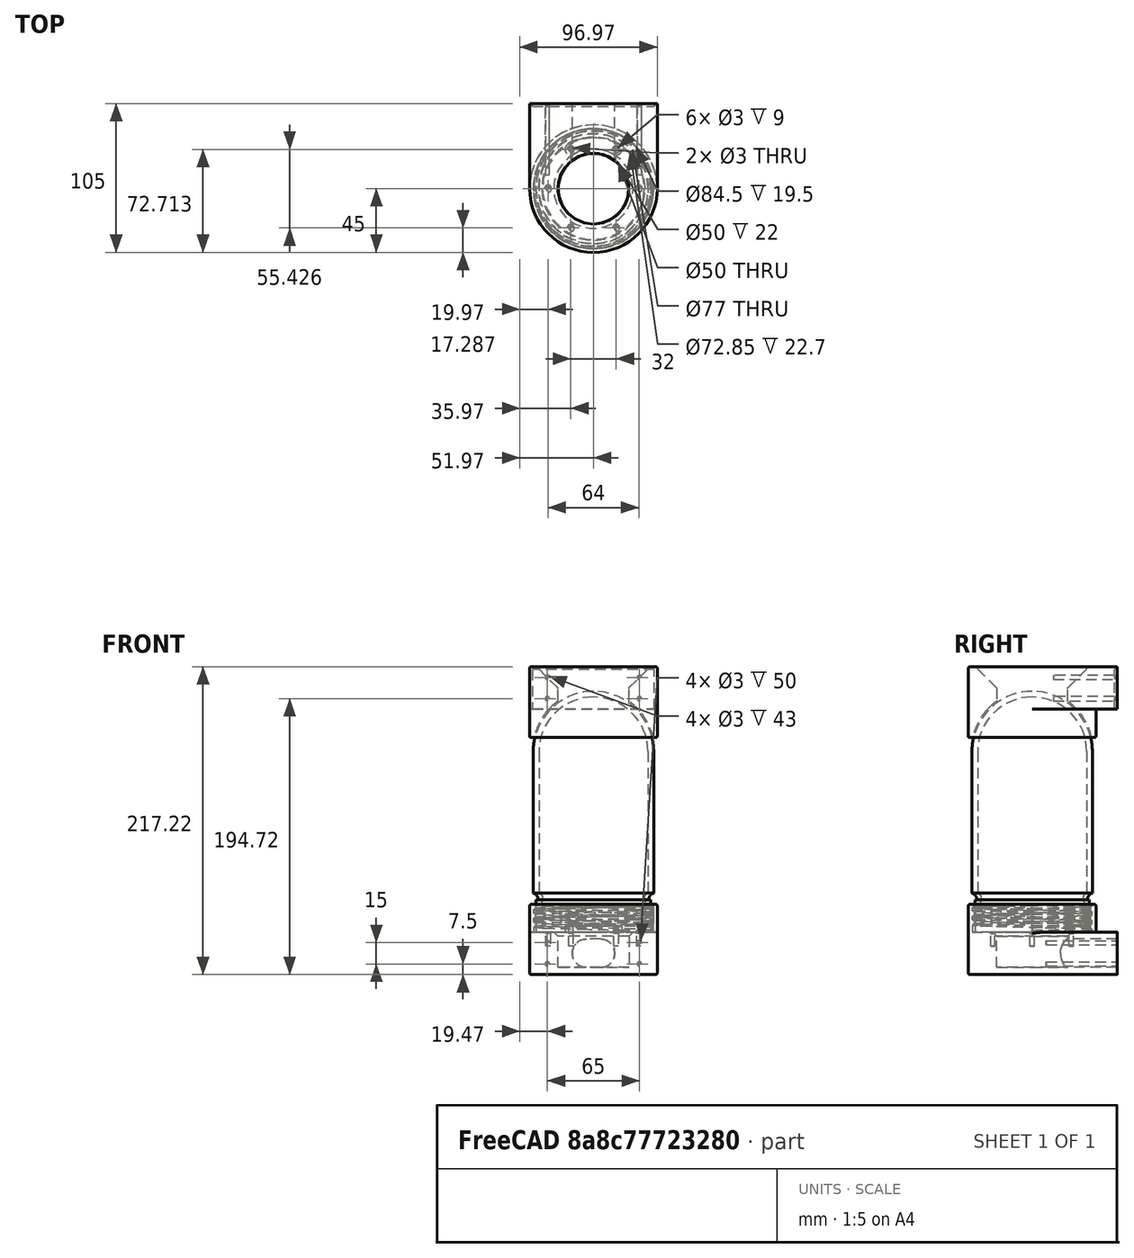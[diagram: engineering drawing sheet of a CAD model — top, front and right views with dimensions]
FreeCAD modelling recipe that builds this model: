
FCSTD DOCUMENT  (FreeCAD 0.19R)
Label: CrocSaintGerard_V3
License: All rights reserved
LicenseURL: http://en.wikipedia.org/wiki/All_rights_reserved
objects: Sketcher::SketchObject×17, PartDesign::Pocket×9, PartDesign::Pad×4, PartDesign::Body×4, PartDesign::Chamfer×3, PartDesign::Fillet×3, PartDesign::Revolution×2, Part::Helix×1, PartDesign::ShapeBinder×1, PartDesign::AdditivePipe×1, PartDesign::LinearPattern×1, Mesh::Feature×1, PartDesign::Groove×1
note: 70 computed .brp shape members not serialized (recipe doc carries the construction recipe); baked Part::Feature solids carry a one-line shape summary decoded from their .brp

FEATURE [Part::Helix] Helix
  Angle = 0
  AttacherType = Attacher::AttachEngine3D
  Height = 6.22
  LocalCoord = 0
  Pitch = 6.23
  Radius = 40.5
  Style = 1
FEATURE [Sketcher::SketchObject] Sketch001  label="sketch_cylindre_base"
  FullyConstrained = true
  MapMode = 5
  Support = -> [XY_Plane]
  sketch-geometry (2):
    g0: Circle CenterX=0 CenterY=0 CenterZ=0 NormalX=0 NormalY=0 NormalZ=1 AngleXU=0 Radius=42.25
    g1: Circle CenterX=0 CenterY=0 CenterZ=0 NormalX=0 NormalY=0 NormalZ=1 AngleXU=0 Radius=45
  constraints (4):
    c: Coincident(g0,g-1)
    c: Coincident(g1,g0)
    c: Radius(g0) = 42.25
    c: Radius(g1) = 45
FEATURE [PartDesign::Pad] Pad  label="cylindre_base"
  Direction = (1,1,1)
  Length = 20
  Length2 = 100
  Profile = -> Sketch001
  Type = 0
FEATURE [Sketcher::SketchObject] Sketch002  label="sketch_profil_dent"
  FullyConstrained = true
  MapMode = 5
  Placement = pos=(0,0,0) rot=(1,0,0;1.5708rad)
  Support = -> [XZ_Plane]
  sketch-geometry (7):
    g0: LineSegment StartX=42.25 StartY=4.40427 StartZ=0 EndX=40.9557 EndY=3.11 EndZ=0
    g1: LineSegment StartX=40.9557 StartY=3.11 StartZ=0 EndX=40.9557 EndY=1.29427 EndZ=0
    g2: LineSegment StartX=40.9557 StartY=1.29427 StartZ=0 EndX=42.25 EndY=0 EndZ=0
    g3: LineSegment StartX=42.25 StartY=4.40427 StartZ=0 EndX=42.25 EndY=6.22 EndZ=0
    g4: LineSegment StartX=42.25 StartY=6.22 StartZ=0 EndX=43.25 EndY=6.22 EndZ=0
    g5: LineSegment StartX=43.25 StartY=6.22 StartZ=0 EndX=43.25 EndY=0 EndZ=0
    g6: LineSegment StartX=43.25 StartY=0 StartZ=0 EndX=42.25 EndY=0 EndZ=0
  constraints (21):
    c: Coincident(g0,g1)
    c: Vertical(g1)
    c: Coincident(g1,g2)
    c: DistanceX(g-2,g2) = 42.25
    c: PointOnObject(g2,g-1)
    c: Coincident(g0,g3)
    c: Vertical(g3)
    c: Coincident(g3,g4)
    c: Horizontal(g4)
    c: Coincident(g4,g5)
    c: PointOnObject(g5,g-1)
    c: Vertical(g5)
    c: Coincident(g5,g6)
    c: Coincident(g6,g2)
    c: DistanceX(g4,g4) = 1
    c: Equal(g3,g1)
    c: Equal(g2,g0)
    c: Angle(g2,g-1) = 0.785398
    c: Equal(g1,g3)
    c: DistanceY(g5,g5) = 6.22
    c: DistanceX(g-2,g0) = 42.25
FEATURE [PartDesign::ShapeBinder] ShapeBinder  label="ShapeBinder-helix"
  Support = -> [Helix]
  TraceSupport = false
FEATURE [PartDesign::AdditivePipe] AdditivePipe  label="filet"
  AuxilleryCurvelinear = true
  AuxillerySpineTangent = false
  BaseFeature = -> Pad
  Binormal = (0,0,0)
  Mode = 2
  Profile = -> Sketch002
  Spine = -> ShapeBinder
  SpineTangent = false
  Transformation = 0
  Transition = 0
FEATURE [PartDesign::LinearPattern] LinearPattern  label="ajout_filets"
  BaseFeature = -> AdditivePipe
  Direction = -> Z_Axis
  Length = 12.46
  Occurrences = 3
  Originals = -> [AdditivePipe]
FEATURE [Sketcher::SketchObject] Sketch003  label="sketch_decoupe_filetage"
  FullyConstrained = true
  MapMode = 5
  Placement = pos=(0,0,0) rot=(1,0,0;1.5708rad)
  Support = -> [XZ_Plane]
  sketch-geometry (4):
    g0: LineSegment StartX=-90 StartY=29.5 StartZ=0 EndX=90 EndY=29.5 EndZ=0
    g1: LineSegment StartX=90 StartY=29.5 StartZ=0 EndX=90 EndY=19.5 EndZ=0
    g2: LineSegment StartX=90 StartY=19.5 StartZ=0 EndX=-90 EndY=19.5 EndZ=0
    g3: LineSegment StartX=-90 StartY=19.5 StartZ=0 EndX=-90 EndY=29.5 EndZ=0
  constraints (11):
    c: Coincident(g0,g1)
    c: Coincident(g1,g2)
    c: Coincident(g2,g3)
    c: Coincident(g3,g0)
    c: Horizontal(g2)
    c: Vertical(g1)
    c: Vertical(g3)
    c: DistanceY(g-1,g1) = 19.5
    c: Symmetric(g0,g0,g-2)
    c: DistanceY(g1,g1) = 10
    c: DistanceX(g0,g0) = 180
FEATURE [PartDesign::Pocket] Pocket  label="decoupe_filetage"
  BaseFeature = -> LinearPattern
  Length = 200
  Length2 = 100
  Midplane = true
  Profile = -> Sketch003
  Type = 0
FEATURE [Sketcher::SketchObject] Sketch008  label="sketch_enceinte_verre"
  FullyConstrained = true
  MapMode = 5
  Support = -> [XY_Plane003]
  sketch-geometry (11):
    g0: ArcOfCircle CenterX=-127.4 CenterY=0 CenterZ=0 NormalX=0 NormalY=0 NormalZ=1 AngleXU=0 Radius=42.5 StartAngle=1.5708 EndAngle=3.14159
    g1: ArcOfCircle CenterX=-127.4 CenterY=0 CenterZ=0 NormalX=0 NormalY=0 NormalZ=1 AngleXU=0 Radius=38.5 StartAngle=1.5708 EndAngle=3.14159
    g2: LineSegment StartX=-127.4 StartY=38.5 StartZ=0 EndX=-27.4 EndY=38.5 EndZ=0
    g3: ArcOfCircle CenterX=-24.2871 CenterY=39.1905 CenterZ=0 NormalX=0 NormalY=0 NormalZ=1 AngleXU=0 Radius=3.18854 StartAngle=3.35987 EndAngle=5.2334
    g4: LineSegment StartX=-22.7 StartY=36.425 StartZ=0 EndX=0 EndY=36.425 EndZ=0
    g5: LineSegment StartX=-127.4 StartY=42.5 StartZ=0 EndX=-27.4 EndY=42.5 EndZ=0
    g6: ArcOfCircle CenterX=-22.7 CenterY=43.802 CenterZ=0 NormalX=0 NormalY=0 NormalZ=1 AngleXU=0 Radius=4.87701 StartAngle=3.41184 EndAngle=4.71239
    g7: LineSegment StartX=-22.7 StartY=38.925 StartZ=0 EndX=-22.7 EndY=40.425 EndZ=0
    g8: LineSegment StartX=-22.7 StartY=40.425 StartZ=0 EndX=0 EndY=40.425 EndZ=0
    g9: LineSegment StartX=0 StartY=40.425 StartZ=0 EndX=0 EndY=36.425 EndZ=0
    g10: LineSegment StartX=-165.9 StartY=4.7e-15 StartZ=0 EndX=-169.9 EndY=5.2e-15 EndZ=0
  constraints (35):
    c: PointOnObject(g0,g-1)
    c: PointOnObject(g0,g-1)
    c: Coincident(g1,g0)
    c: PointOnObject(g1,g-1)
    c: Angle(g1) = 1.5708
    c: Angle(g0) = 1.5708
    c: Tangent(g1,g2) = 1.5708
    c: Coincident(g3,g2)
    c: Coincident(g4,g3)
    c: PointOnObject(g4,g-2)
    c: Horizontal(g4)
    c: Coincident(g5,g0)
    c: Horizontal(g5)
    c: Coincident(g6,g5)
    c: Coincident(g6,g7)
    c: Coincident(g7,g8)
    c: PointOnObject(g8,g-2)
    c: Horizontal(g8)
    c: Coincident(g8,g9)
    c: Coincident(g9,g4)
    c: Coincident(g10,g0)
    c: DistanceX(g10,g10) = 4
    c: Radius(g0) = 42.5
    c: Coincident(g1,g10)
    c: DistanceY(g9,g9) = 4
    c: Perpendicular(g6,g7)
    c: Vertical(g7)
    c: DistanceY(g-1,g4) = 36.425
    c: Equal(g4,g8)
    c: DistanceX(g8,g8) = 22.7
    c: DistanceX(g-2,g5) = -27.4
    c: Equal(g2,g5)
    c: PointOnObject(g3,g6)
    c: DistanceY(g7,g7) = 1.5
    c: DistanceX(g5,g5) = 100
FEATURE [PartDesign::Revolution] Revolution  label="revolution_enceinte_verre"
  AllowMultiFace = false
  Angle = 360
  Axis = (1,0,0)
  Base = (0,0,0)
  Profile = -> Sketch008
  ReferenceAxis = -> Sketch008 [H_Axis]
FEATURE [PartDesign::Body] Body003  label="enceinte_verre"
  Group = -> [Sketch008,Revolution]
  Origin = -> Origin003
  Placement = pos=(-3.8e-15,0,-1.78e-14) rot=(0,1,0;1.5708rad)
  Tip = -> Revolution
FEATURE [Sketcher::SketchObject] Sketch  label="sketch_base"
  ExternalGeometry = -> [Pocket]
  FullyConstrained = true
  MapMode = 5
  Placement = pos=(0,0,0) rot=(1,0,0;3.14159rad)
  Support = -> [Pocket]
  sketch-geometry (4):
    g0: ArcOfCircle CenterX=0 CenterY=0 CenterZ=0 NormalX=0 NormalY=0 NormalZ=1 AngleXU=0 Radius=45 StartAngle=0 EndAngle=3.14159
    g1: LineSegment StartX=-45 StartY=5.5e-15 StartZ=0 EndX=-45 EndY=-60 EndZ=0
    g2: LineSegment StartX=-45 StartY=-60 StartZ=0 EndX=45 EndY=-60 EndZ=0
    g3: LineSegment StartX=45 StartY=-60 StartZ=0 EndX=45 EndY=0 EndZ=0
  constraints (11):
    c: Coincident(g0,g-1)
    c: PointOnObject(g0,g-1)
    c: PointOnObject(g0,g-1)
    c: Tangent(g0,g1) = -1.5708
    c: Coincident(g1,g2)
    c: Horizontal(g2)
    c: Coincident(g2,g3)
    c: Coincident(g3,g0)
    c: Vertical(g3)
    c: Radius(g0) = 45
    c: DistanceY(g1,g1) = 60
FEATURE [PartDesign::Pad] Pad001  label="base"
  BaseFeature = -> Pocket
  Direction = (1,1,1)
  Length = 30
  Length2 = 100
  Profile = -> Sketch
  Type = 0
FEATURE [Sketcher::SketchObject] Sketch009  label="sketch_passage_fils"
  FullyConstrained = true
  MapMode = 5
  Support = -> [Pad001]
  sketch-geometry (1):
    g0: Circle CenterX=0 CenterY=0 CenterZ=0 NormalX=0 NormalY=0 NormalZ=1 AngleXU=0 Radius=25
  constraints (2):
    c: Coincident(g0,g-1)
    c: Radius(g0) = 25
FEATURE [PartDesign::Pocket] Pocket001  label="passage_fils"
  BaseFeature = -> Pad001
  Length = 25
  Length2 = 100
  Profile = -> Sketch009
  Type = 0
FEATURE [Sketcher::SketchObject] Sketch010  label="sketch_passage_fils_vertical"
  ExternalGeometry = -> [Pocket001]
  FullyConstrained = true
  MapMode = 5
  Placement = pos=(0,60,0) rot=(0,0.707107,0.707107;3.14159rad)
  Support = -> [Pocket001]
  sketch-geometry (4):
    g0: ArcOfCircle CenterX=-5 CenterY=-15 CenterZ=0 NormalX=0 NormalY=0 NormalZ=1 AngleXU=0 Radius=10 StartAngle=1.5708 EndAngle=4.71239
    g1: ArcOfCircle CenterX=5 CenterY=-15 CenterZ=0 NormalX=0 NormalY=0 NormalZ=1 AngleXU=0 Radius=10 StartAngle=4.71239 EndAngle=7.85398
    g2: LineSegment StartX=-5 StartY=-25 StartZ=0 EndX=5 EndY=-25 EndZ=0
    g3: LineSegment StartX=-5 StartY=-5 StartZ=0 EndX=5 EndY=-5 EndZ=0
  constraints (9):
    c: Tangent(g0,g3) = 1.5708
    c: Tangent(g0,g2) = -1.5708
    c: Tangent(g2,g1) = -1.5708
    c: Tangent(g3,g1) = 1.5708
    c: Equal(g0,g1)
    c: Symmetric(g0,g1,g-2)
    c: Distance(g1,g-3) = 5
    c: DistanceY(g-1,g1) = -5
    c: DistanceX(g2,g2) = 10
FEATURE [PartDesign::Pocket] Pocket002  label="passage_fils_vertical"
  BaseFeature = -> Pocket001
  Length = 60
  Length2 = 100
  Profile = -> Sketch010
  Type = 0
FEATURE [Sketcher::SketchObject] Sketch011  label="sketch_vis_fixation"
  ExternalGeometry = -> [Pocket002]
  FullyConstrained = true
  MapMode = 5
  Placement = pos=(0,60,0) rot=(0,0.707107,0.707107;3.14159rad)
  Support = -> [Pocket002]
  sketch-geometry (4):
    g0: Circle CenterX=-32.5 CenterY=-7.5 CenterZ=0 NormalX=0 NormalY=0 NormalZ=1 AngleXU=0 Radius=1.5
    g1: Circle CenterX=32.5 CenterY=-7.5 CenterZ=0 NormalX=0 NormalY=0 NormalZ=1 AngleXU=0 Radius=1.5
    g2: Circle CenterX=-32.5 CenterY=-22.5 CenterZ=0 NormalX=0 NormalY=0 NormalZ=1 AngleXU=0 Radius=1.5
    g3: Circle CenterX=32.5 CenterY=-22.5 CenterZ=0 NormalX=0 NormalY=0 NormalZ=1 AngleXU=0 Radius=1.5
  constraints (10):
    c: Symmetric(g1,g0,g-2)
    c: DistanceY(g-1,g0) = -7.5
    c: Distance(g0,g1) = 65
    c: Radius(g0) = 1.5
    c: Equal(g0,g1)
    c: Symmetric(g3,g2,g-2)
    c: Radius(g2) = 1.5
    c: Equal(g2,g3)
    c: Distance(g3,g2) = 65
    c: Distance(g3,g-3) = 7.5
FEATURE [PartDesign::Pocket] Pocket003  label="vis_fixation"
  BaseFeature = -> Pocket002
  Length = 50
  Length2 = 100
  Profile = -> Sketch011
  Type = 0
FEATURE [PartDesign::Chamfer] Chamfer
  Angle = 45
  Base = -> Pocket003 [Edge95]
  BaseFeature = -> Pocket003
  ChamferType = 0
  FlipDirection = false
  Size = 3
  Size2 = 1
  SupportTransform = false
FEATURE [Sketcher::SketchObject] Sketch012  label="sketch_vis_montage_interieur"
  FullyConstrained = true
  MapMode = 5
  Support = -> [Chamfer]
  sketch-geometry (13):
    g0: LineSegment StartX=-16 StartY=27.7128 StartZ=0 EndX=-32 EndY=-3.3857e-12 EndZ=0
    g1: LineSegment StartX=-32 StartY=-3.3857e-12 StartZ=0 EndX=-16 EndY=-27.7128 EndZ=0
    g2: LineSegment StartX=-16 StartY=-27.7128 StartZ=0 EndX=16 EndY=-27.7128 EndZ=0
    g3: LineSegment StartX=16 StartY=-27.7128 StartZ=0 EndX=32 EndY=9.738e-12 EndZ=0
    g4: LineSegment StartX=32 StartY=9.738e-12 StartZ=0 EndX=16 EndY=27.7128 EndZ=0
    g5: LineSegment StartX=16 StartY=27.7128 StartZ=0 EndX=-16 EndY=27.7128 EndZ=0
    g6: Circle CenterX=0 CenterY=0 CenterZ=0 NormalX=0 NormalY=0 NormalZ=1 AngleXU=0 Radius=32
    g7: Circle CenterX=-16 CenterY=27.7128 CenterZ=0 NormalX=0 NormalY=0 NormalZ=1 AngleXU=0 Radius=1.5
    g8: Circle CenterX=16 CenterY=27.7128 CenterZ=0 NormalX=0 NormalY=0 NormalZ=1 AngleXU=0 Radius=1.5
    g9: Circle CenterX=-32 CenterY=-3.3857e-12 CenterZ=0 NormalX=0 NormalY=0 NormalZ=1 AngleXU=0 Radius=1.5
    g10: Circle CenterX=32 CenterY=9.738e-12 CenterZ=0 NormalX=0 NormalY=0 NormalZ=1 AngleXU=0 Radius=1.5
    g11: Circle CenterX=16 CenterY=-27.7128 CenterZ=0 NormalX=0 NormalY=0 NormalZ=1 AngleXU=0 Radius=1.5
    g12: Circle CenterX=-16 CenterY=-27.7128 CenterZ=0 NormalX=0 NormalY=0 NormalZ=1 AngleXU=0 Radius=1.5
  constraints (28):
    c: Coincident(g0,g1)
    c: Coincident(g1,g2)
    c: Coincident(g2,g3)
    c: Coincident(g3,g4)
    c: Coincident(g4,g5)
    c: Coincident(g5,g0)
    c: Equal(g0, g1-g5) x5
    c: PointOnObject(g0,g6)
    c: PointOnObject(g1,g6)
    c: PointOnObject(g2,g6)
    c: PointOnObject(g3,g6)
    c: PointOnObject(g4,g6)
    c: PointOnObject(g5,g6)
    c: Coincident(g6,g-1)
    c: Horizontal(g5)
    c: Radius(g6) = 32
    c: Coincident(g7,g0)
    c: Coincident(g8,g4)
    c: Coincident(g9,g0)
    c: Coincident(g10,g3)
    c: Coincident(g11,g2)
    c: Coincident(g12,g1)
    c: Radius(g11) = 1.5
    c: Equal(g11,g12)
    c: Equal(g11,g9)
    c: Equal(g11,g7)
    c: Equal(g11,g8)
    c: Equal(g11,g10)
FEATURE [PartDesign::Pocket] Pocket004  label="vis_montage_interieur"
  BaseFeature = -> Chamfer
  Length = 10
  Length2 = 100
  Profile = -> Sketch012
  Type = 0
FEATURE [PartDesign::Chamfer] Chamfer001
  Angle = 45
  Base = -> Pocket004 [Edge3,Edge2,Edge4,Edge6,Edge8,Edge7]
  BaseFeature = -> Pocket004
  ChamferType = 0
  FlipDirection = false
  Size = 1
  Size2 = 1
  SupportTransform = false
FEATURE [Mesh::Feature] Mesh  label="fixation_enceinte_verre (Meshed)"
FEATURE [Sketcher::SketchObject] Sketch013
  FullyConstrained = true
  MapMode = 5
  Placement = pos=(0,0,0) rot=(0.57735,0.57735,0.57735;2.0944rad)
  Support = -> [YZ_Plane004]
  sketch-geometry (4):
    g0: ArcOfCircle CenterX=0 CenterY=128 CenterZ=0 NormalX=0 NormalY=0 NormalZ=1 AngleXU=0 Radius=43 StartAngle=2.39448 EndAngle=2.92551
    g1: LineSegment StartX=-42 StartY=137.22 StartZ=0 EndX=-45 EndY=137.22 EndZ=0
    g2: LineSegment StartX=-45 StartY=137.22 StartZ=0 EndX=-45 EndY=157.22 EndZ=0
    g3: LineSegment StartX=-45 StartY=157.22 StartZ=0 EndX=-31.5471 EndY=157.22 EndZ=0
  constraints (13):
    c: PointOnObject(g0,g-2)
    c: Coincident(g0,g1)
    c: Coincident(g1,g2)
    c: Vertical(g2)
    c: Coincident(g2,g3)
    c: Coincident(g3,g0)
    c: Horizontal(g3)
    c: Horizontal(g1)
    c: Radius(g0) = 43
    c: DistanceY(g2,g2) = 20
    c: DistanceX(g-2,g1) = -45
    c: DistanceY(g-1,g0) = 128
    c: DistanceX(g1,g1) = 3
FEATURE [PartDesign::Revolution] Revolution001
  Angle = 360
  Axis = (-2e-16,3e-16,1)
  Base = (0,0,0)
  Placement = pos=(0,0,0) rot=(0.57735,0.57735,0.57735;2.0944rad)
  Profile = -> Sketch013
  ReferenceAxis = -> Sketch013 [V_Axis]
FEATURE [Sketcher::SketchObject] Sketch014
  ExternalGeometry = -> [Revolution001]
  FullyConstrained = true
  MapMode = 5
  Placement = pos=(-8.73e-14,6.11e-14,157.22) rot=(0,0,-1;1.5708rad)
  Support = -> [Revolution001]
  sketch-geometry (4):
    g0: ArcOfCircle CenterX=0 CenterY=0 CenterZ=0 NormalX=0 NormalY=0 NormalZ=1 AngleXU=0 Radius=45 StartAngle=4.71239 EndAngle=7.85398
    g1: LineSegment StartX=1.38e-14 StartY=45 StartZ=0 EndX=-60 EndY=45 EndZ=0
    g2: LineSegment StartX=-60 StartY=45 StartZ=0 EndX=-60 EndY=-45 EndZ=0
    g3: LineSegment StartX=-60 StartY=-45 StartZ=0 EndX=-7.1e-15 EndY=-45 EndZ=0
  constraints (10):
    c: Coincident(g0,g-1)
    c: PointOnObject(g0,g-3)
    c: PointOnObject(g0,g-2)
    c: PointOnObject(g0,g-2)
    c: Tangent(g0,g1) = -1.5708
    c: Coincident(g1,g2)
    c: Coincident(g2,g3)
    c: Coincident(g3,g0)
    c: Symmetric(g2,g1,g-1)
    c: DistanceX(g-2,g1) = -60
FEATURE [PartDesign::Pad] Pad002
  BaseFeature = -> Revolution001
  Direction = (1,1,1)
  Length = 30
  Length2 = 100
  Placement = pos=(0,0,0) rot=(0.57735,0.57735,0.57735;2.0944rad)
  Profile = -> Sketch014
  Type = 0
FEATURE [Sketcher::SketchObject] Sketch015
  ExternalGeometry = -> [Pad002]
  FullyConstrained = true
  MapMode = 5
  Placement = pos=(0,0,0) rot=(0.57735,0.57735,0.57735;2.0944rad)
  Support = -> [YZ_Plane004]
  sketch-geometry (3):
    g0: ArcOfCircle CenterX=2.84e-14 CenterY=128 CenterZ=0 NormalX=0 NormalY=0 NormalZ=1 AngleXU=0 Radius=43 StartAngle=1.5708 EndAngle=2.39448
    g1: LineSegment StartX=-31.5471 StartY=157.22 StartZ=0 EndX=3.6e-15 EndY=157.22 EndZ=0
    g2: LineSegment StartX=2.4e-15 StartY=157.22 StartZ=0 EndX=2.4e-15 EndY=171 EndZ=0
  constraints (8):
    c: Coincident(g0,g-3)
    c: Coincident(g0,g-3)
    c: PointOnObject(g0,g-2)
    c: Coincident(g0,g1)
    c: Coincident(g1,g2)
    c: Coincident(g2,g0)
    c: Vertical(g2)
    c: Horizontal(g1)
FEATURE [PartDesign::Groove] Groove
  Angle = 360
  Axis = (-2e-16,3e-16,1)
  Base = (0,0,0)
  BaseFeature = -> Pad002
  Placement = pos=(0,0,0) rot=(0.57735,0.57735,0.57735;2.0944rad)
  Profile = -> Sketch015
  ReferenceAxis = -> Sketch015 [V_Axis]
  Reversed = true
FEATURE [Sketcher::SketchObject] Sketch016
  FullyConstrained = true
  MapMode = 5
  Placement = pos=(-2.43e-13,1.236e-13,187.22) rot=(0,0,-1;1.5708rad)
  Support = -> [Groove]
  sketch-geometry (1):
    g0: Circle CenterX=0 CenterY=0 CenterZ=0 NormalX=0 NormalY=0 NormalZ=1 AngleXU=0 Radius=25
  constraints (2):
    c: Coincident(g0,g-1)
    c: Radius(g0) = 25
FEATURE [PartDesign::Pocket] Pocket005
  BaseFeature = -> Groove
  Length = 43
  Length2 = 100
  Placement = pos=(0,0,0) rot=(0.57735,0.57735,0.57735;2.0944rad)
  Profile = -> Sketch016
  Type = 0
FEATURE [PartDesign::Chamfer] Chamfer002
  Angle = 45
  Base = -> Pocket005 [Edge11]
  BaseFeature = -> Pocket005
  ChamferType = 0
  FlipDirection = false
  Placement = pos=(0,0,0) rot=(0.57735,0.57735,0.57735;2.0944rad)
  Size = 15
  Size2 = 1
  SupportTransform = false
FEATURE [Sketcher::SketchObject] Sketch017
  ExternalGeometry = -> [Chamfer002]
  FullyConstrained = true
  MapMode = 5
  Placement = pos=(2.66e-14,60,-6.99e-14) rot=(0.57735,0.57735,0.57735;4.18879rad)
  Support = -> [Chamfer002]
  sketch-geometry (4):
    g0: Circle CenterX=164.72 CenterY=32.5 CenterZ=0 NormalX=0 NormalY=0 NormalZ=1 AngleXU=0 Radius=1.5
    g1: Circle CenterX=179.72 CenterY=32.5 CenterZ=0 NormalX=0 NormalY=0 NormalZ=1 AngleXU=0 Radius=1.5
    g2: Circle CenterX=164.72 CenterY=-32.5 CenterZ=0 NormalX=0 NormalY=0 NormalZ=1 AngleXU=0 Radius=1.5
    g3: Circle CenterX=179.72 CenterY=-32.5 CenterZ=0 NormalX=0 NormalY=0 NormalZ=1 AngleXU=0 Radius=1.5
  constraints (10):
    c: Radius(g0) = 1.5
    c: Equal(g0,g1)
    c: Equal(g0,g3)
    c: Equal(g0,g2)
    c: Symmetric(g0,g2,g-1)
    c: Symmetric(g3,g1,g-1)
    c: Distance(g1,g3) = 65
    c: Distance(g0,g2) = 65
    c: Distance(g0,g-3) = 7.5
    c: Distance(g3,g-4) = 7.5
FEATURE [PartDesign::Pocket] Pocket006
  BaseFeature = -> Chamfer002
  Length = 45
  Length2 = 100
  Placement = pos=(0,0,0) rot=(0.57735,0.57735,0.57735;2.0944rad)
  Profile = -> Sketch017
  Type = 0
FEATURE [PartDesign::Fillet] Fillet
  Base = -> Chamfer001 [Edge116,Edge168,Edge182,Edge171,Edge181,Edge166]
  BaseFeature = -> Chamfer001
  Radius = 1
  SupportTransform = false
FEATURE [PartDesign::Body] Body  label="fixation_enceinte_verre"
  Group = -> [Sketch001,Pad,Sketch002,ShapeBinder,AdditivePipe,LinearPattern,Sketch003,Pocket,Sketch,Pad001,Sketch009,Pocket001,Sketch010,Pocket002,Sketch011,Pocket003,Chamfer,Sketch012,Pocket004,Chamfer001,Fillet]
  Origin = -> Origin
  Tip = -> Fillet
FEATURE [PartDesign::Fillet] Fillet001
  Base = -> Pocket006 [Edge10,Edge19,Edge27]
  BaseFeature = -> Pocket006
  Placement = pos=(0,0,0) rot=(0.57735,0.57735,0.57735;2.0944rad)
  Radius = 1
  SupportTransform = false
FEATURE [PartDesign::Fillet] Fillet002
  Base = -> Fillet001 [Edge5,Edge22,Edge42]
  BaseFeature = -> Fillet001
  Placement = pos=(0,0,0) rot=(0.57735,0.57735,0.57735;2.0944rad)
  Radius = 1
  SupportTransform = false
FEATURE [Sketcher::SketchObject] Sketch018
  ExternalGeometry = -> [Fillet002]
  FullyConstrained = true
  MapMode = 5
  Placement = pos=(2.66e-14,60,-8.99e-14) rot=(0.57735,0.57735,0.57735;4.18879rad)
  Support = -> [Fillet002]
  sketch-geometry (4):
    g0: LineSegment StartX=155.22 StartY=43 StartZ=0 EndX=185.22 EndY=43 EndZ=0
    g1: LineSegment StartX=185.22 StartY=43 StartZ=0 EndX=185.22 EndY=-43 EndZ=0
    g2: LineSegment StartX=185.22 StartY=-43 StartZ=0 EndX=155.22 EndY=-43 EndZ=0
    g3: LineSegment StartX=155.22 StartY=-43 StartZ=0 EndX=155.22 EndY=43 EndZ=0
  constraints (11):
    c: Coincident(g0,g1)
    c: Coincident(g1,g2)
    c: Coincident(g2,g3)
    c: Coincident(g3,g0)
    c: Horizontal(g0)
    c: Horizontal(g2)
    c: Vertical(g3)
    c: Symmetric(g1,g0,g-1)
    c: Distance(g0,g-3) = 2
    c: Distance(g0,g-4) = 2
    c: Distance(g0,g-5) = 2
FEATURE [PartDesign::Pocket] Pocket007
  BaseFeature = -> Fillet002
  Length = 2
  Length2 = 100
  Placement = pos=(0,0,0) rot=(0.57735,0.57735,0.57735;2.0944rad)
  Profile = -> Sketch018
  Type = 0
FEATURE [PartDesign::Body] Body004  label="tete"
  Group = -> [Sketch013,Revolution001,Sketch014,Pad002,Sketch015,Groove,Sketch016,Pocket005,Chamfer002,Sketch017,Pocket006,Fillet001,Fillet002,Sketch018,Pocket007]
  Origin = -> Origin004
  Tip = -> Pocket007
FEATURE [Sketcher::SketchObject] Sketch019
  FullyConstrained = true
  MapMode = 5
  Support = -> [XY_Plane005]
  sketch-geometry (4):
    g0: ArcOfCircle CenterX=-1.9e-15 CenterY=0 CenterZ=0 NormalX=0 NormalY=0 NormalZ=1 AngleXU=0 Radius=28 StartAngle=1.0472 EndAngle=2.0944
    g1: ArcOfCircle CenterX=-1.9e-15 CenterY=0 CenterZ=0 NormalX=0 NormalY=0 NormalZ=1 AngleXU=0 Radius=36 StartAngle=1.0472 EndAngle=2.0944
    g2: ArcOfCircle CenterX=-16 CenterY=27.7128 CenterZ=0 NormalX=0 NormalY=0 NormalZ=1 AngleXU=0 Radius=4 StartAngle=2.0944 EndAngle=5.23599
    g3: ArcOfCircle CenterX=16 CenterY=27.7128 CenterZ=0 NormalX=0 NormalY=0 NormalZ=1 AngleXU=0 Radius=4 StartAngle=4.18879 EndAngle=7.33038
  constraints (11):
    c: Symmetric(g0,g0,g-2)
    c: Coincident(g1,g0)
    c: Symmetric(g1,g1,g-2)
    c: Coincident(g3,g1)
    c: Tangent(g2,g0) = 1.5708
    c: Tangent(g2,g1) = -1.5708
    c: Tangent(g3,g0) = 1.5708
    c: Coincident(g0,g-1)
    c: Radius(g1) = 36
    c: Radius(g0) = 28
    c: Angle(g0) = 1.0472
FEATURE [PartDesign::Pad] Pad003
  Direction = (1,1,1)
  Length = 4
  Length2 = 100
  Profile = -> Sketch019
  Type = 0
FEATURE [Sketcher::SketchObject] Sketch020
  ExternalGeometry = -> [Pad003]
  FullyConstrained = true
  MapMode = 5
  Placement = pos=(0,0,4) rot=(0,0,1;0rad)
  Support = -> [Pad003]
  sketch-geometry (2):
    g0: Circle CenterX=-16 CenterY=27.7128 CenterZ=0 NormalX=0 NormalY=0 NormalZ=1 AngleXU=0 Radius=1.5
    g1: Circle CenterX=16 CenterY=27.7128 CenterZ=0 NormalX=0 NormalY=0 NormalZ=1 AngleXU=0 Radius=1.5
  constraints (4):
    c: Coincident(g0,g-3)
    c: Coincident(g1,g-4)
    c: Radius(g1) = 1.5
    c: Equal(g1,g0)
FEATURE [PartDesign::Pocket] Pocket008
  BaseFeature = -> Pad003
  Length = 5
  Length2 = 100
  Profile = -> Sketch020
  Type = 0
FEATURE [PartDesign::Body] Body005  label="support_interieur"
  Group = -> [Sketch019,Pad003,Sketch020,Pocket008]
  Origin = -> Origin005
  Tip = -> Pocket008
